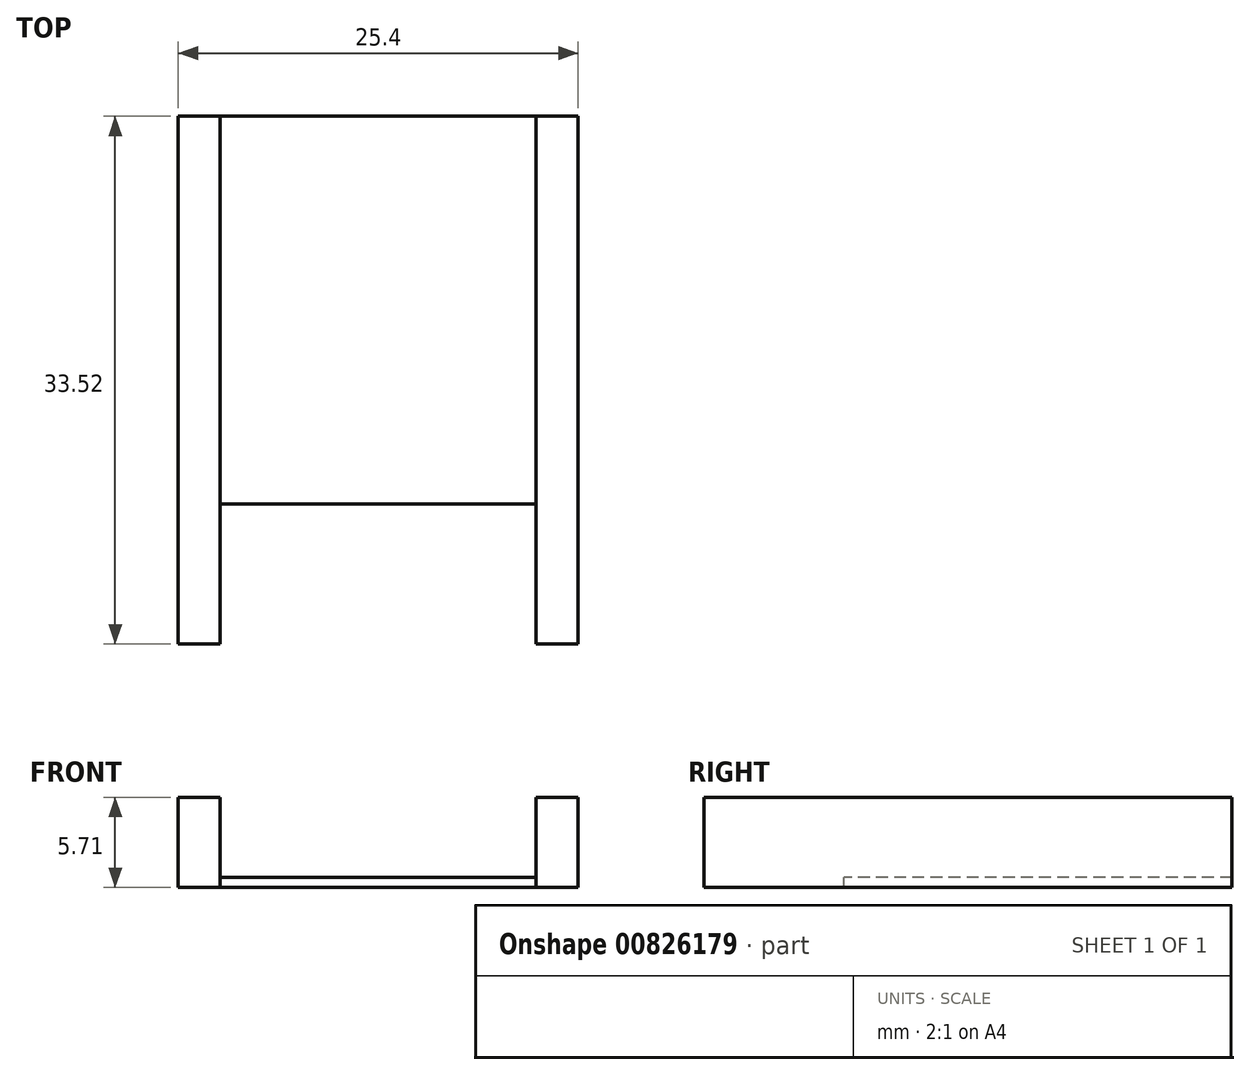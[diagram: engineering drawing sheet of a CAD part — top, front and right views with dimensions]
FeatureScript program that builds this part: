
annotation { "Feature Type Name" : "Feature", "Feature Type Description" : "" }
export const myFeature = defineFeature(function(context is Context, id is Id, definition is map)
    precondition{}
    {
        {
            var Q0;
            Q0=qCreatedBy(makeId("Top.planeOp"),FACE);
            var sketch = newSketch(context, id + "F0", { "sketchPlane" : qUnion([Q0])});
            skLineSegment(sketch, "E0.bottom", {"start": v(-12.7, 16.76) * mm, "end": v(12.7, 16.76) * mm});
            skLineSegment(sketch, "E0.top", {"start": v(-12.7, -16.76) * mm, "end": v(12.7, -16.76) * mm});
            skLineSegment(sketch, "E0.left", {"start": v(-12.7, 16.76) * mm, "end": v(-12.7, -16.76) * mm});
            skLineSegment(sketch, "E0.right", {"start": v(12.7, 16.76) * mm, "end": v(12.7, -16.76) * mm});
            skPoint(sketch, "E0.middle", {"position": v(0, 0) * mm});
            skSolve(sketch);
        }
        {
            var Q0;
            Q0=makeQuery(id+"F0.imprint","IMPRINT",FACE,{"disambiguationData":[TD([[makeQuery(id+"F0.imprint","IMPRINT",EDGE,{"derivedFrom":sQuery(id+"F0.wireOp",EDGE,"E0.bottom")}),-1.0]])]});
            extrude(context, id + "F1", {"entities" : qUnion([Q0]), "depth" : 5.7 * mm, "offsetDistance" : 25.4 * mm});
        }
        {
            var Q0;
            Q0=makeQuery(id+"F1.opExtrude","CAP_FACE",FACE,{"disambiguationData":[OSD([sQuery(id+"F0.wireOp",EDGE,"E0.bottom"),sQuery(id+"F0.wireOp",EDGE,"E0.top"),sQuery(id+"F0.wireOp",EDGE,"E0.left"),sQuery(id+"F0.wireOp",EDGE,"E0.right")])],"isStart":false});
            var sketch = newSketch(context, id + "F2", { "sketchPlane" : qUnion([Q0])});
            skSolve(sketch);
        }
        {
            var Q0;
            Q0=makeQuery(id+"F2.imprint","IMPRINT",FACE,{"disambiguationData":[TD([[makeQuery(id+"F2.imprint","IMPRINT",EDGE,{"derivedFrom":makeQuery(id+"F1.opExtrude","CAP_EDGE",EDGE,{"disambiguationData":[OSD([sQuery(id+"F0.wireOp",EDGE,"E0.bottom")])],"isStart":false})}),-1.0]])]});
            var sketch = newSketch(context, id + "F3", { "sketchPlane" : qUnion([Q0])});
            skLineSegment(sketch, "E1.bottom", {"start": v(10.03, 16.83) * mm, "end": v(-10.03, 16.83) * mm});
            skLineSegment(sketch, "E1.top", {"start": v(10.03, -16.83) * mm, "end": v(-10.03, -16.83) * mm});
            skLineSegment(sketch, "E1.left", {"start": v(10.03, 16.83) * mm, "end": v(10.03, -16.83) * mm});
            skLineSegment(sketch, "E1.right", {"start": v(-10.03, 16.83) * mm, "end": v(-10.03, -16.83) * mm});
            skPoint(sketch, "E1.middle", {"position": v(0, 0) * mm});
            skSolve(sketch);
        }
        {
            var Q0;
            Q0 = qSketchRegion(id + "F3", true);
            extrude(context, id + "F4", {"entities" : qUnion([Q0]), "operationType" : NewBodyOperationType.REMOVE, "oppositeDirection" : true, "depth" : 5.08 * mm, "offsetDistance" : 25.4 * mm});
        }
        {
            var Q0;
            Q0=makeQuery(id+"F4.boolean.opBoolean","COPY",FACE,{"derivedFrom":makeQuery(id+"F4.opExtrude","CAP_FACE",FACE,{"disambiguationData":[OSD([sQuery(id+"F3.wireOp",EDGE,"E1.bottom"),sQuery(id+"F3.wireOp",EDGE,"E1.top"),sQuery(id+"F3.wireOp",EDGE,"E1.left"),sQuery(id+"F3.wireOp",EDGE,"E1.right")])],"isStart":false})});
            var sketch = newSketch(context, id + "F5", { "sketchPlane" : qUnion([Q0])});
            skLineSegment(sketch, "E2.bottom", {"start": v(-10.03, -16.76) * mm, "end": v(10.03, -16.76) * mm});
            skLineSegment(sketch, "E2.top", {"start": v(-10.03, -7.87) * mm, "end": v(10.03, -7.87) * mm});
            skLineSegment(sketch, "E2.left", {"start": v(-10.03, -16.76) * mm, "end": v(-10.03, -7.87) * mm});
            skLineSegment(sketch, "E2.right", {"start": v(10.03, -16.76) * mm, "end": v(10.03, -7.87) * mm});
            skSolve(sketch);
        }
        {
            var Q0;
            Q0 = qSketchRegion(id + "F5", true);
            extrude(context, id + "F6", {"entities" : qUnion([Q0]), "operationType" : NewBodyOperationType.REMOVE, "oppositeDirection" : true, "depth" : 25.4 * mm, "offsetDistance" : 25.4 * mm});
        }
    });
